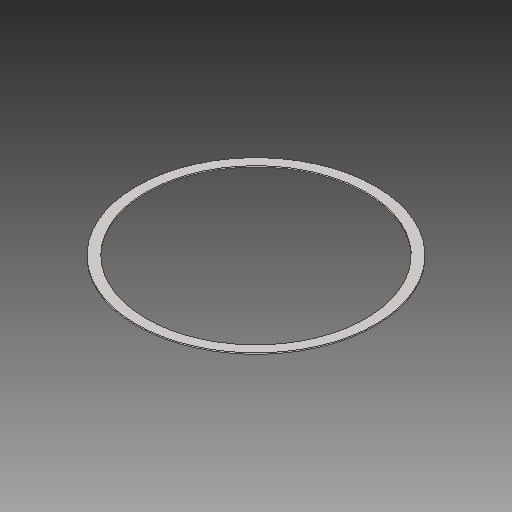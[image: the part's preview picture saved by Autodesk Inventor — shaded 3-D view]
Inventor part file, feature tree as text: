
AUTODESK INVENTOR PART (.ipt)
format: ipt  version: 2017 (Build 210142000, 142)  size: 105,472 bytes
history: native  units: in
note: dims shown in document units (in); Inventor stores cm internally (conversion verified against a paired STEP export)
features: extrude x1, sketch x1
ambient origin geometry x8: Origin, YZ Plane, XZ Plane, XY Plane, X Axis, Y Axis, Z Axis, Center Point
bodies: Solid1 (feature_tree)
feature tree (2):
  extrude  "Extrusion1"  Depth=0.0625in
  sketch  "Sketch1"  dims[d0=11.9713in d1=10.989in d2=0.0625in d3=0.0in]
